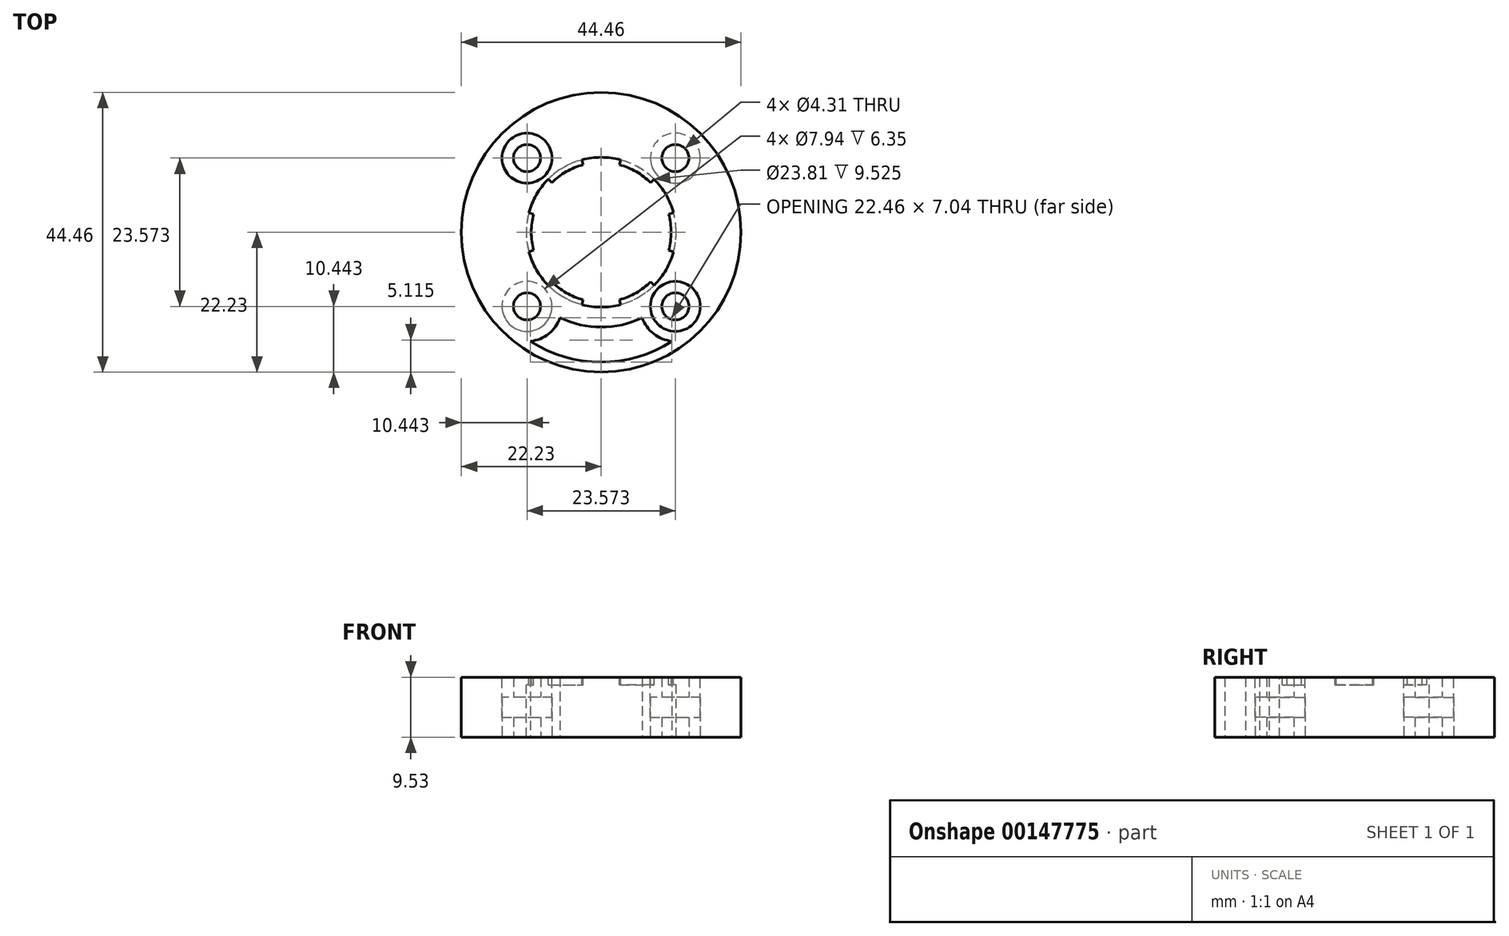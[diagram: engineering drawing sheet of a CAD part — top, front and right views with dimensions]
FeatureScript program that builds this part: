
annotation { "Feature Type Name" : "Feature", "Feature Type Description" : "" }
export const myFeature = defineFeature(function(context is Context, id is Id, definition is map)
    precondition{}
    {
        {
            var Q0;
            Q0=qCreatedBy(makeId("Top.planeOp"),FACE);
            var sketch = newSketch(context, id + "F0", { "sketchPlane" : qUnion([Q0])});
            skCircle(sketch, "E0", {"center": v(0, 0) * mm, "radius": 11.11 * mm});
            skLineSegment(sketch, "E1.bottom", {"start": v(11.79, 11.79) * mm, "end": v(-11.79, 11.79) * mm, "construction": true});
            skLineSegment(sketch, "E1.top", {"start": v(11.79, -11.79) * mm, "end": v(-11.79, -11.79) * mm, "construction": true});
            skLineSegment(sketch, "E1.left", {"start": v(11.79, 11.79) * mm, "end": v(11.79, -11.79) * mm, "construction": true});
            skLineSegment(sketch, "E1.right", {"start": v(-11.79, 11.79) * mm, "end": v(-11.79, -11.79) * mm, "construction": true});
            skCircle(sketch, "E2", {"center": v(-11.79, 11.79) * mm, "radius": 5.56 * mm, "construction": true});
            skLineSegment(sketch, "E3", {"start": v(0, 0) * mm, "end": v(0, 11.11) * mm});
            skCircle(sketch, "E4", {"center": v(-11.79, 11.79) * mm, "radius": 2.15 * mm});
            skCircle(sketch, "E5", {"center": v(-11.79, -11.79) * mm, "radius": 2.15 * mm});
            skCircle(sketch, "E6", {"center": v(11.79, -11.79) * mm, "radius": 2.15 * mm});
            skCircle(sketch, "E7", {"center": v(11.79, 11.79) * mm, "radius": 2.15 * mm});
            skCircle(sketch, "E8", {"center": v(0, 0) * mm, "radius": 22.23 * mm});
            skSolve(sketch);
        }
        {
            var Q0;
            Q0=qSketchRegion(id+"F0",true);
            extrude(context, id + "F1", {"entities" : qUnion([Q0]), "depth" : 9.52 * mm});
        }
        {
            var Q0;
            Q0=makeQuery(id+"F1.opExtrude","CAP_FACE",FACE,{"disambiguationData":[OSD([sQuery(id+"F0.wireOp",EDGE,"E0"),sQuery(id+"F0.wireOp",EDGE,"66XUYhlC-g5MV-aD6u-Z0ay-hjDTK084ohIY.top"),sQuery(id+"F0.wireOp",EDGE,"66XUYhlC-g5MV-aD6u-Z0ay-hjDTK084ohIY.left"),sQuery(id+"F0.wireOp",EDGE,"66XUYhlC-g5MV-aD6u-Z0ay-hjDTK084ohIY.right"),sQuery(id+"F0.wireOp",EDGE,"nqN0bBuQ-hJ1m-BtXy-d5jW-CiUxEReohyUV"),sQuery(id+"F0.wireOp",EDGE,"E4"),sQuery(id+"F0.wireOp",EDGE,"E5"),sQuery(id+"F0.wireOp",EDGE,"E6"),sQuery(id+"F0.wireOp",EDGE,"E7")])],"isStart":false});
            var sketch = newSketch(context, id + "F2", { "sketchPlane" : qUnion([Q0])});
            skLineSegment(sketch, "E9", {"start": v(0, 0) * mm, "end": v(0, 11.11) * mm, "construction": true});
            skLineSegment(sketch, "E10", {"start": v(0, 0) * mm, "end": v(2.88, 10.73) * mm, "construction": true});
            skLineSegment(sketch, "E11", {"start": v(0, 0) * mm, "end": v(-2.88, 10.73) * mm, "construction": true});
            skArc(sketch, "E12", {"start": v(2.88, 10.73) * mm, "mid": v(0, 11.11) * mm, "end": v(-2.88, 10.73) * mm});
            skLineSegment(sketch, "E13", {"start": v(-2.88, 10.73) * mm, "end": v(-3.08, 11.5) * mm});
            skLineSegment(sketch, "E14", {"start": v(2.88, 10.73) * mm, "end": v(3.08, 11.5) * mm});
            skArc(sketch, "E15", {"start": v(3.08, 11.5) * mm, "mid": v(0, 11.9) * mm, "end": v(-3.08, 11.5) * mm});
            skSolve(sketch);
        }
        {
            var Q0;
            Q0=qSketchRegion(id+"F2",true);
            var Q1;
            Q1=makeQuery(id+"F1.opExtrude","CAP_FACE",FACE,{"disambiguationData":[OSD([sQuery(id+"F0.wireOp",EDGE,"E0"),sQuery(id+"F0.wireOp",EDGE,"66XUYhlC-g5MV-aD6u-Z0ay-hjDTK084ohIY.top"),sQuery(id+"F0.wireOp",EDGE,"66XUYhlC-g5MV-aD6u-Z0ay-hjDTK084ohIY.left"),sQuery(id+"F0.wireOp",EDGE,"66XUYhlC-g5MV-aD6u-Z0ay-hjDTK084ohIY.right"),sQuery(id+"F0.wireOp",EDGE,"nqN0bBuQ-hJ1m-BtXy-d5jW-CiUxEReohyUV"),sQuery(id+"F0.wireOp",EDGE,"E4"),sQuery(id+"F0.wireOp",EDGE,"E5"),sQuery(id+"F0.wireOp",EDGE,"E6"),sQuery(id+"F0.wireOp",EDGE,"E7")])],"isStart":true});
            extrude(context, id + "F3", {"entities" : qUnion([Q0]), "operationType" : NewBodyOperationType.REMOVE, "endBound" : BoundingType.UP_TO_SURFACE, "oppositeDirection" : true, "endBoundEntityFace" : qUnion([Q1]), "depth" : 25.4 * mm});
        }
        {
            var Q0;
            Q0=makeQuery(id+"F3.boolean.opBoolean","COPY",FACE,{"derivedFrom":makeQuery(id+"F3.opExtrude","SWEPT_FACE",FACE,{"disambiguationData":[OSD([sQuery(id+"F2.wireOp",EDGE,"E15")])]})});
            var Q1;
            Q1=makeQuery(id+"F3.boolean.opBoolean","COPY",FACE,{"derivedFrom":makeQuery(id+"F3.opExtrude","SWEPT_FACE",FACE,{"disambiguationData":[OSD([sQuery(id+"F2.wireOp",EDGE,"E13")])]})});
            var Q2;
            Q2=makeQuery(id+"F3.boolean.opBoolean","COPY",FACE,{"derivedFrom":makeQuery(id+"F3.opExtrude","SWEPT_FACE",FACE,{"disambiguationData":[OSD([sQuery(id+"F2.wireOp",EDGE,"E14")])]})});
            var Q3;
            Q3=makeQuery(id+"F1.opExtrude","SWEPT_FACE",FACE,{"disambiguationData":[OSD([sQuery(id+"F0.wireOp",EDGE,"E0")])]});
            circularPattern(context, id + "F4", {"patternType" : PatternType.FACE, "faces" : qUnion([Q0, Q1, Q2]), "axis" : qUnion([Q3]), "angle" : 60 * degree, "instanceCount" : 6});
        }
        {
            var Q0;
            Q0=makeQuery(id+"F1.opExtrude","CAP_FACE",FACE,{"disambiguationData":[OSD([sQuery(id+"F0.wireOp",EDGE,"E0"),sQuery(id+"F0.wireOp",EDGE,"E4"),sQuery(id+"F0.wireOp",EDGE,"E5"),sQuery(id+"F0.wireOp",EDGE,"E6"),sQuery(id+"F0.wireOp",EDGE,"E7"),sQuery(id+"F0.wireOp",EDGE,"E8")])],"isStart":false});
            cPlane(context, id + "F5", {"entities" : qUnion([Q0]), "cplaneType" : CPlaneType.OFFSET, "offset" : 1.23 * mm, "oppositeDirection" : true, "width" : 152.4 * mm, "height" : 152.4 * mm});
        }
        {
            var Q0;
            Q0=makeQuery(id+"F1.opExtrude","CAP_FACE",FACE,{"disambiguationData":[OSD([sQuery(id+"F0.wireOp",EDGE,"E0"),sQuery(id+"F0.wireOp",EDGE,"E4"),sQuery(id+"F0.wireOp",EDGE,"E5"),sQuery(id+"F0.wireOp",EDGE,"E6"),sQuery(id+"F0.wireOp",EDGE,"E7"),sQuery(id+"F0.wireOp",EDGE,"E8")])],"isStart":true});
            var sketch = newSketch(context, id + "F6", { "sketchPlane" : qUnion([Q0])});
            skCircle(sketch, "E16", {"center": v(0, 0) * mm, "radius": 11.9 * mm});
            skSolve(sketch);
        }
        {
            var Q0;
            Q0=qSketchRegion(id+"F6",true);
            var Q1;
            Q1=qCreatedBy(id+"F5.planeOp",FACE);
            extrude(context, id + "F7", {"entities" : qUnion([Q0]), "operationType" : NewBodyOperationType.REMOVE, "endBound" : BoundingType.UP_TO_SURFACE, "oppositeDirection" : true, "endBoundEntityFace" : qUnion([Q1]), "depth" : 25.4 * mm});
        }
        {
            var Q0;
            Q0=makeQuery(id+"F1.opExtrude","CAP_FACE",FACE,{"disambiguationData":[OSD([sQuery(id+"F0.wireOp",EDGE,"E0"),sQuery(id+"F0.wireOp",EDGE,"E4"),sQuery(id+"F0.wireOp",EDGE,"E5"),sQuery(id+"F0.wireOp",EDGE,"E6"),sQuery(id+"F0.wireOp",EDGE,"E7"),sQuery(id+"F0.wireOp",EDGE,"E8")])],"isStart":true});
            cPlane(context, id + "F8", {"entities" : qUnion([Q0]), "cplaneType" : CPlaneType.OFFSET, "offset" : 3.17 * mm, "oppositeDirection" : true, "width" : 152.4 * mm, "height" : 152.4 * mm});
        }
        {
            var Q0;
            Q0=makeQuery(id+"F1.opExtrude","CAP_FACE",FACE,{"disambiguationData":[OSD([sQuery(id+"F0.wireOp",EDGE,"E0"),sQuery(id+"F0.wireOp",EDGE,"E4"),sQuery(id+"F0.wireOp",EDGE,"E5"),sQuery(id+"F0.wireOp",EDGE,"E6"),sQuery(id+"F0.wireOp",EDGE,"E7"),sQuery(id+"F0.wireOp",EDGE,"E8")])],"isStart":false});
            cPlane(context, id + "F9", {"entities" : qUnion([Q0]), "cplaneType" : CPlaneType.OFFSET, "offset" : 3.17 * mm, "oppositeDirection" : true, "width" : 152.4 * mm, "height" : 152.4 * mm});
        }
        {
            var Q0;
            Q0=makeQuery(id+"F1.opExtrude","CAP_FACE",FACE,{"disambiguationData":[OSD([sQuery(id+"F0.wireOp",EDGE,"E0"),sQuery(id+"F0.wireOp",EDGE,"E4"),sQuery(id+"F0.wireOp",EDGE,"E5"),sQuery(id+"F0.wireOp",EDGE,"E6"),sQuery(id+"F0.wireOp",EDGE,"E7"),sQuery(id+"F0.wireOp",EDGE,"E8")])],"isStart":true});
            var sketch = newSketch(context, id + "F10", { "sketchPlane" : qUnion([Q0])});
            skCircle(sketch, "E17", {"center": v(11.79, -11.79) * mm, "radius": 3.97 * mm});
            skCircle(sketch, "E18", {"center": v(-11.79, 11.79) * mm, "radius": 3.97 * mm});
            skSolve(sketch);
        }
        {
            var Q0;
            Q0=qSketchRegion(id+"F10",true);
            var Q1;
            Q1=qCreatedBy(id+"F9.planeOp",FACE);
            extrude(context, id + "F11", {"entities" : qUnion([Q0]), "operationType" : NewBodyOperationType.REMOVE, "endBound" : BoundingType.UP_TO_SURFACE, "oppositeDirection" : true, "endBoundEntityFace" : qUnion([Q1]), "depth" : 25.4 * mm});
        }
        {
            var Q0;
            Q0=makeQuery(id+"F1.opExtrude","CAP_FACE",FACE,{"disambiguationData":[OSD([sQuery(id+"F0.wireOp",EDGE,"E0"),sQuery(id+"F0.wireOp",EDGE,"E4"),sQuery(id+"F0.wireOp",EDGE,"E5"),sQuery(id+"F0.wireOp",EDGE,"E6"),sQuery(id+"F0.wireOp",EDGE,"E7"),sQuery(id+"F0.wireOp",EDGE,"E8")])],"isStart":false});
            var sketch = newSketch(context, id + "F12", { "sketchPlane" : qUnion([Q0])});
            skCircle(sketch, "E19", {"center": v(-11.79, 11.79) * mm, "radius": 3.97 * mm});
            skCircle(sketch, "E20", {"center": v(11.79, -11.79) * mm, "radius": 3.97 * mm});
            skSolve(sketch);
        }
        {
            var Q0;
            Q0=qSketchRegion(id+"F12",true);
            var Q1;
            Q1=qCreatedBy(id+"F8.planeOp",FACE);
            extrude(context, id + "F13", {"entities" : qUnion([Q0]), "operationType" : NewBodyOperationType.REMOVE, "endBound" : BoundingType.UP_TO_SURFACE, "oppositeDirection" : true, "endBoundEntityFace" : qUnion([Q1]), "depth" : 25.4 * mm});
        }
        {
            var Q0;
            Q0=makeQuery(id+"F1.opExtrude","CAP_FACE",FACE,{"disambiguationData":[OSD([sQuery(id+"F0.wireOp",EDGE,"E0"),sQuery(id+"F0.wireOp",EDGE,"E4"),sQuery(id+"F0.wireOp",EDGE,"E5"),sQuery(id+"F0.wireOp",EDGE,"E6"),sQuery(id+"F0.wireOp",EDGE,"E7"),sQuery(id+"F0.wireOp",EDGE,"E8")])],"isStart":true});
            var sketch = newSketch(context, id + "F14", { "sketchPlane" : qUnion([Q0])});
            skArc(sketch, "E21", {"start": v(-6.53, 13.6) * mm, "mid": v(-8.34, 16.14) * mm, "end": v(-11.23, 17.31) * mm});
            skArc(sketch, "E22", {"start": v(11.23, 17.31) * mm, "mid": v(0, 20.64) * mm, "end": v(-11.23, 17.31) * mm});
            skArc(sketch, "E23", {"start": v(11.23, 17.31) * mm, "mid": v(8.34, 16.14) * mm, "end": v(6.53, 13.6) * mm});
            skArc(sketch, "E24", {"start": v(6.53, 13.6) * mm, "mid": v(0, 15.08) * mm, "end": v(-6.53, 13.6) * mm});
            skSolve(sketch);
        }
        {
            var Q0;
            Q0=qSketchRegion(id+"F14",true);
            var Q1;
            Q1=makeQuery(id+"F1.opExtrude","CAP_FACE",FACE,{"disambiguationData":[OSD([sQuery(id+"F0.wireOp",EDGE,"E0"),sQuery(id+"F0.wireOp",EDGE,"E4"),sQuery(id+"F0.wireOp",EDGE,"E5"),sQuery(id+"F0.wireOp",EDGE,"E6"),sQuery(id+"F0.wireOp",EDGE,"E7"),sQuery(id+"F0.wireOp",EDGE,"E8")])],"isStart":false});
            extrude(context, id + "F15", {"entities" : qUnion([Q0]), "operationType" : NewBodyOperationType.REMOVE, "endBound" : BoundingType.UP_TO_SURFACE, "oppositeDirection" : true, "endBoundEntityFace" : qUnion([Q1]), "depth" : 25.4 * mm});
        }
    });
